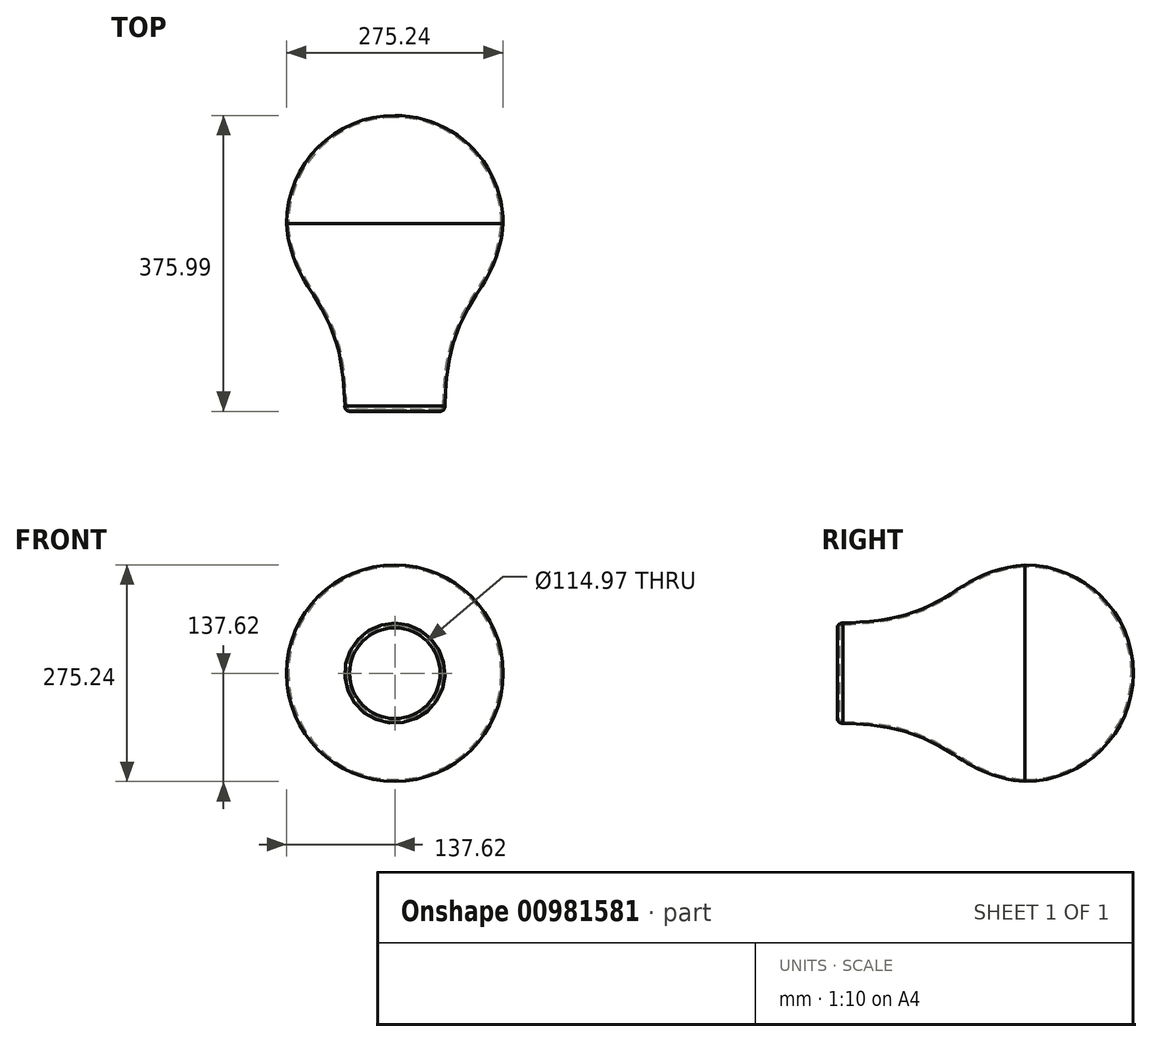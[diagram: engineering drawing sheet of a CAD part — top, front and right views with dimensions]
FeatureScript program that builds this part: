
annotation { "Feature Type Name" : "Feature", "Feature Type Description" : "" }
export const myFeature = defineFeature(function(context is Context, id is Id, definition is map)
    precondition{}
    {
        {
            var Q0;
            Q0=qCreatedBy(makeId("Top.planeOp"),FACE);
            var sketch = newSketch(context, id + "F0", { "sketchPlane" : qUnion([Q0])});
            skLineSegment(sketch, "E0", {"start": v(0, 137.62) * mm, "end": v(0, -238.37) * mm});
            skArc(sketch, "E1", {"start": v(0, 137.62) * mm, "mid": v(97.31, 97.31) * mm, "end": v(137.62, 0) * mm});
            skLineSegment(sketch, "E2", {"start": v(0, -238.37) * mm, "end": v(57.49, -238.37) * mm});
            skFitSpline(sketch, "E3", {"points": [v(137.62, 0) * mm, v(121.5, -60.05) * mm, v(96.22, -101.9) * mm, v(71.8, -160.32) * mm, v(63.53, -231.44) * mm], "startDerivative": vector(-17.04, -253.34) * mm, "endDerivative": vector(-11.72, -240.36) * mm});
            skArc(sketch, "E4", {"start": v(57.49, -238.37) * mm, "mid": v(62.08, -236.28) * mm, "end": v(63.53, -231.44) * mm});
            skSolve(sketch);
        }
        {
            var Q0;
            Q0=makeQuery(id+"F0.imprint","IMPRINT",FACE,{"disambiguationData":[TD([[makeQuery(id+"F0.imprint","IMPRINT",EDGE,{"derivedFrom":sQuery(id+"F0.wireOp",EDGE,"E0")}),1.0]])]});
            var Q1;
            Q1=sQuery(id+"F0.wireOp",EDGE,"E0");
            revolve(context, id + "F1", {"surfaceOperationType" : NewSurfaceOperationType.NEW, "entities" : qUnion([Q0]), "axis" : qUnion([Q1]), "revolveType" : RevolveType.FULL});
        }
        {
            var Q0;
            Q0=makeQuery(id+"F1.opRevolve","SWEPT_FACE",FACE,{"disambiguationData":[OSD([sQuery(id+"F0.wireOp",EDGE,"E2")])]});
            shell(context, id + "F2", {"entities" : qUnion([Q0]), "thickness" : 2.54 * mm});
        }
    });
